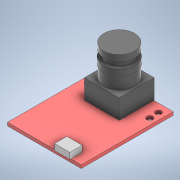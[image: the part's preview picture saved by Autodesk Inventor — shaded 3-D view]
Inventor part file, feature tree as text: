
AUTODESK INVENTOR PART (.ipt)
format: ipt  version: 2020 (Build 240168000, 168)  size: 202,240 bytes
history: native  units: mm
features: extrude x7, sketch x7, projected_geometry x6, other x1
ambient origin geometry x8: Origin, YZ Plane, XZ Plane, XY Plane, X Axis, Y Axis, Z Axis, Center Point
bodies: Body1 (feature_tree)
feature tree (21):
  other  "Твердое тело1"
  extrude  "Выдавливание1"  Depth=36.0mm
  extrude  "Выдавливание2"  Depth=45.0mm
  extrude  "Выдавливание3"  Depth=3.0mm
  extrude  "Выдавливание4"  Depth=30.0mm
  extrude  "Выдавливание5"  Depth=8.5mm
  extrude  "Выдавливание6"  Depth=2.8mm
  extrude  "Выдавливание7"  Depth=29.5mm
  sketch  "Эскиз1"
  sketch  "Эскиз2"
  projected_geometry  "Спроецированная петля1"
  sketch  "Эскиз3"
  projected_geometry  "Спроецированная петля2"
  sketch  "Эскиз4"
  projected_geometry  "Спроецированная петля3"
  sketch  "Эскиз5"
  projected_geometry  "Спроецированная петля4"
  sketch  "Эскиз6"
  projected_geometry  "Спроецированная петля5"
  sketch  "Эскиз7"
  projected_geometry  "Спроецированная петля6"
